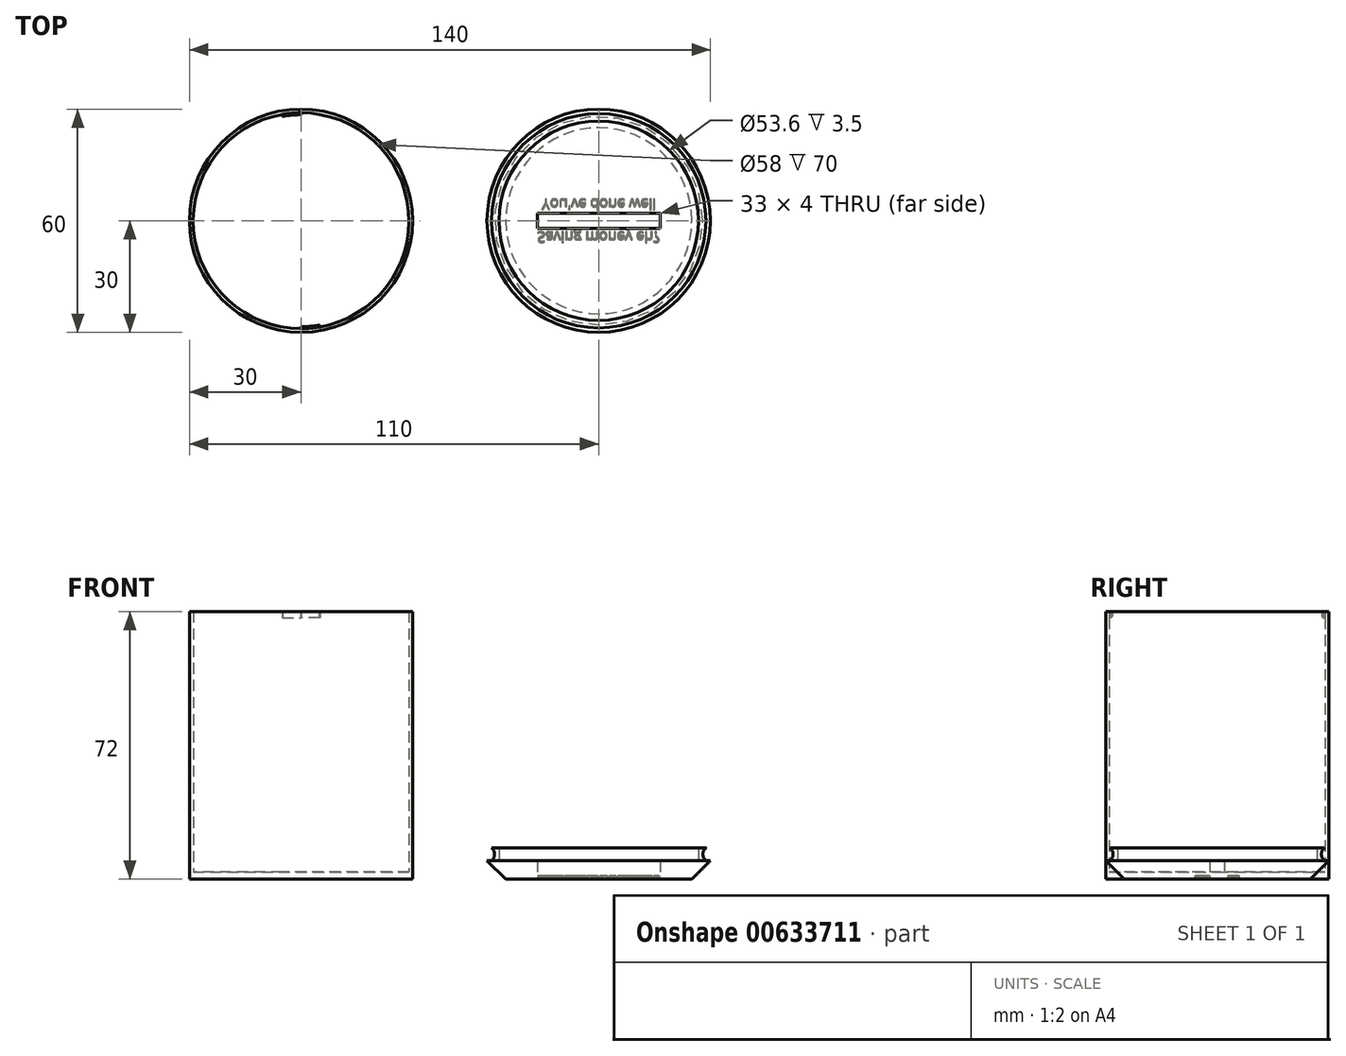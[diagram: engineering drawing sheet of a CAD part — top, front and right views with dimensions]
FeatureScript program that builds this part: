
annotation { "Feature Type Name" : "Feature", "Feature Type Description" : "" }
export const myFeature = defineFeature(function(context is Context, id is Id, definition is map)
    precondition{}
    {
        {
            var Q0;
            Q0=qCreatedBy(makeId("Top.planeOp"),FACE);
            var sketch = newSketch(context, id + "F0", { "sketchPlane" : qUnion([Q0])});
            skCircle(sketch, "E0", {"center": v(0, 0) * mm, "radius": 30 * mm});
            skSolve(sketch);
        }
        {
            var Q0;
            Q0=makeQuery(id+"F0.imprint","IMPRINT",FACE,{"disambiguationData":[TD([[makeQuery(id+"F0.imprint","IMPRINT",EDGE,{"derivedFrom":sQuery(id+"F0.wireOp",EDGE,"E0")}),1.0]])]});
            extrude(context, id + "F1", {"entities" : qUnion([Q0]), "depth" : 2 * mm, "offsetDistance" : 25 * mm});
        }
        {
            var Q0;
            Q0=makeQuery(id+"F1.opExtrude","CAP_FACE",FACE,{"disambiguationData":[OSD([sQuery(id+"F0.wireOp",EDGE,"E0")])],"isStart":false});
            var sketch = newSketch(context, id + "F2", { "sketchPlane" : qUnion([Q0])});
            skCircle(sketch, "E1", {"center": v(0, 0) * mm, "radius": 29 * mm});
            skSolve(sketch);
        }
        {
            var Q0;
            Q0=makeQuery(id+"F2.imprint","IMPRINT",FACE,{"disambiguationData":[TD([[makeQuery(id+"F2.imprint","IMPRINT",EDGE,{"derivedFrom":sQuery(id+"F2.wireOp",EDGE,"E1")}),-1.0]])]});
            extrude(context, id + "F3", {"entities" : qUnion([Q0]), "operationType" : NewBodyOperationType.ADD, "depth" : 70 * mm, "offsetDistance" : 25 * mm});
        }
        {
            var Q0;
            Q0=qCreatedBy(makeId("Right.planeOp"),FACE);
            var sketch = newSketch(context, id + "F4", { "sketchPlane" : qUnion([Q0])});
            skArc(sketch, "E2", {"start": v(-29, 70.27) * mm, "mid": v(-28.5, 71.13) * mm, "end": v(-29, 72) * mm});
            skLineSegment(sketch, "E3", {"start": v(-29, 72) * mm, "end": v(-29, 70.27) * mm});
            skLineSegment(sketch, "E4", {"start": v(0, 0) * mm, "end": v(0, 72) * mm, "construction": true});
            skLineSegment(sketch, "E5.MirrorCS", {"start": v(29, 72) * mm, "end": v(29, 70.27) * mm});
            skArc(sketch, "E6.MirrorCS", {"start": v(29, 70.27) * mm, "mid": v(28.5, 71.13) * mm, "end": v(29, 72) * mm});
            skSolve(sketch);
        }
        {
            var Q0;
            Q0 = qSketchRegion(id + "F4", true);
            var Q1;
            Q1=makeQuery(id+"F3.opExtrude","CAP_EDGE",EDGE,{"disambiguationData":[OSD([sQuery(id+"F2.wireOp",EDGE,"E1")])],"isStart":false});
            revolve(context, id + "F5", {"operationType" : NewBodyOperationType.ADD, "surfaceOperationType" : NewSurfaceOperationType.NEW, "entities" : qUnion([Q0]), "axis" : qUnion([Q1]), "revolveType" : RevolveType.ONE_DIRECTION, "angle" : 10 * degree});
        }
        {
            var Q0;
            Q0=qCreatedBy(makeId("Top.planeOp"),FACE);
            var sketch = newSketch(context, id + "F6", { "sketchPlane" : qUnion([Q0])});
            skLineSegment(sketch, "E7", {"start": v(0, 0) * mm, "end": v(80, 0) * mm, "construction": true});
            skCircle(sketch, "E8", {"center": v(80, 0) * mm, "radius": 25 * mm});
            skSolve(sketch);
        }
        {
            var Q0;
            Q0=makeQuery(id+"F6.imprint","IMPRINT",FACE,{"disambiguationData":[TD([[makeQuery(id+"F6.imprint","IMPRINT",EDGE,{"derivedFrom":sQuery(id+"F6.wireOp",EDGE,"E8")}),1.0]])]});
            extrude(context, id + "F7", {"entities" : qUnion([Q0]), "depth" : 5 * mm, "offsetDistance" : 25 * mm, "hasDraft" : true, "draftAngle" : 45 * degree});
        }
        {
            var Q0;
            Q0=makeQuery(id+"F7.opExtrude","CAP_FACE",FACE,{"disambiguationData":[OSD([sQuery(id+"F6.wireOp",EDGE,"E8")])],"isStart":true});
            var sketch = newSketch(context, id + "F8", { "sketchPlane" : qUnion([Q0])});
            skLineSegment(sketch, "E9.bottom", {"start": v(63.5, -2) * mm, "end": v(96.5, -2) * mm});
            skLineSegment(sketch, "E9.top", {"start": v(63.5, 2) * mm, "end": v(96.5, 2) * mm});
            skLineSegment(sketch, "E9.left", {"start": v(63.5, -2) * mm, "end": v(63.5, 2) * mm});
            skLineSegment(sketch, "E9.right", {"start": v(96.5, -2) * mm, "end": v(96.5, 2) * mm});
            skPoint(sketch, "E9.middle", {"position": v(80, 0) * mm});
            skSolve(sketch);
        }
        {
            var Q0;
            Q0 = qSketchRegion(id + "F8", true);
            extrude(context, id + "F9", {"entities" : qUnion([Q0]), "operationType" : NewBodyOperationType.REMOVE, "endBound" : BoundingType.THROUGH_ALL, "oppositeDirection" : true, "depth" : 25 * mm, "offsetDistance" : 25 * mm});
        }
        {
            var Q0;
            Q0=makeQuery(id+"F7.opExtrude","CAP_FACE",FACE,{"disambiguationData":[OSD([sQuery(id+"F6.wireOp",EDGE,"E8")])],"isStart":false});
            var sketch = newSketch(context, id + "F10", { "sketchPlane" : qUnion([Q0])});
            skCircle(sketch, "E10", {"center": v(80, 0) * mm, "radius": 28.8 * mm});
            skCircle(sketch, "E11", {"center": v(80, 0) * mm, "radius": 26.8 * mm});
            skSolve(sketch);
        }
        {
            var Q0;
            Q0=makeQuery(id+"F10.imprint","IMPRINT",FACE,{"disambiguationData":[TD([[makeQuery(id+"F10.imprint","IMPRINT",EDGE,{"derivedFrom":sQuery(id+"F10.wireOp",EDGE,"E10")}),1.0]])]});
            extrude(context, id + "F11", {"entities" : qUnion([Q0]), "operationType" : NewBodyOperationType.ADD, "depth" : 3.5 * mm, "offsetDistance" : 25 * mm});
        }
        {
            var Q0;
            Q0=qCreatedBy(makeId("Front.planeOp"),FACE);
            var sketch = newSketch(context, id + "F12", { "sketchPlane" : qUnion([Q0])});
            skLineSegment(sketch, "E12", {"start": v(108.8, 5) * mm, "end": v(108.8, 8.49) * mm});
            skArc(sketch, "E13", {"start": v(108.8, 8.49) * mm, "mid": v(108, 6.74) * mm, "end": v(108.8, 5) * mm});
            skLineSegment(sketch, "E14", {"start": v(80, 0) * mm, "end": v(80, 5) * mm, "construction": true});
            skLineSegment(sketch, "E15", {"start": v(108.8, 5) * mm, "end": v(80, 5) * mm, "construction": true});
            skSolve(sketch);
        }
        {
            var Q0;
            Q0 = qSketchRegion(id + "F12", true);
            var Q1;
            Q1=makeQuery(id+"F11.opExtrude","CAP_EDGE",EDGE,{"disambiguationData":[OSD([sQuery(id+"F10.wireOp",EDGE,"E10")])],"isStart":false});
            revolve(context, id + "F13", {"operationType" : NewBodyOperationType.REMOVE, "entities" : qUnion([Q0]), "axis" : qUnion([Q1]), "revolveType" : RevolveType.FULL, "oppositeDirection" : true});
        }
        {
            var Q0;
            Q0=makeQuery(id+"F7.opExtrude","CAP_FACE",FACE,{"disambiguationData":[OSD([sQuery(id+"F6.wireOp",EDGE,"E8")])],"isStart":true});
            var sketch = newSketch(context, id + "F14", { "sketchPlane" : qUnion([Q0])});
            skText(sketch, "E16", { "text": "Saving money eh?", "fontName": "OpenSans-Regular.ttf"});
            skText(sketch, "E17", { "text": "You\'ve done well", "fontName": "OpenSans-Regular.ttf"});
            skLineSegment(sketch, "E18", {"start": v(96.5, 3) * mm, "end": v(96.5, 2) * mm, "construction": true});
            skLineSegment(sketch, "E19", {"start": v(63.5, 3) * mm, "end": v(63.5, 2) * mm, "construction": true});
            skLineSegment(sketch, "E20", {"start": v(80, -2) * mm, "end": v(80, -3) * mm, "construction": true});
            const initialGuessF14  = {"E16": [0.0635, 0.003, 1, 0, 0.00283], "E17": [0.06468, -0.00583, 1, 0, 0.00283]};
            skSetInitialGuess(sketch, initialGuessF14);
            skSolve(sketch);
        }
        {
            var Q0;
            Q0 = qSketchRegion(id + "F14", true);
            extrude(context, id + "F15", {"entities" : qUnion([Q0]), "operationType" : NewBodyOperationType.REMOVE, "oppositeDirection" : true, "depth" : 1 * mm, "offsetDistance" : 25 * mm});
        }
    });
